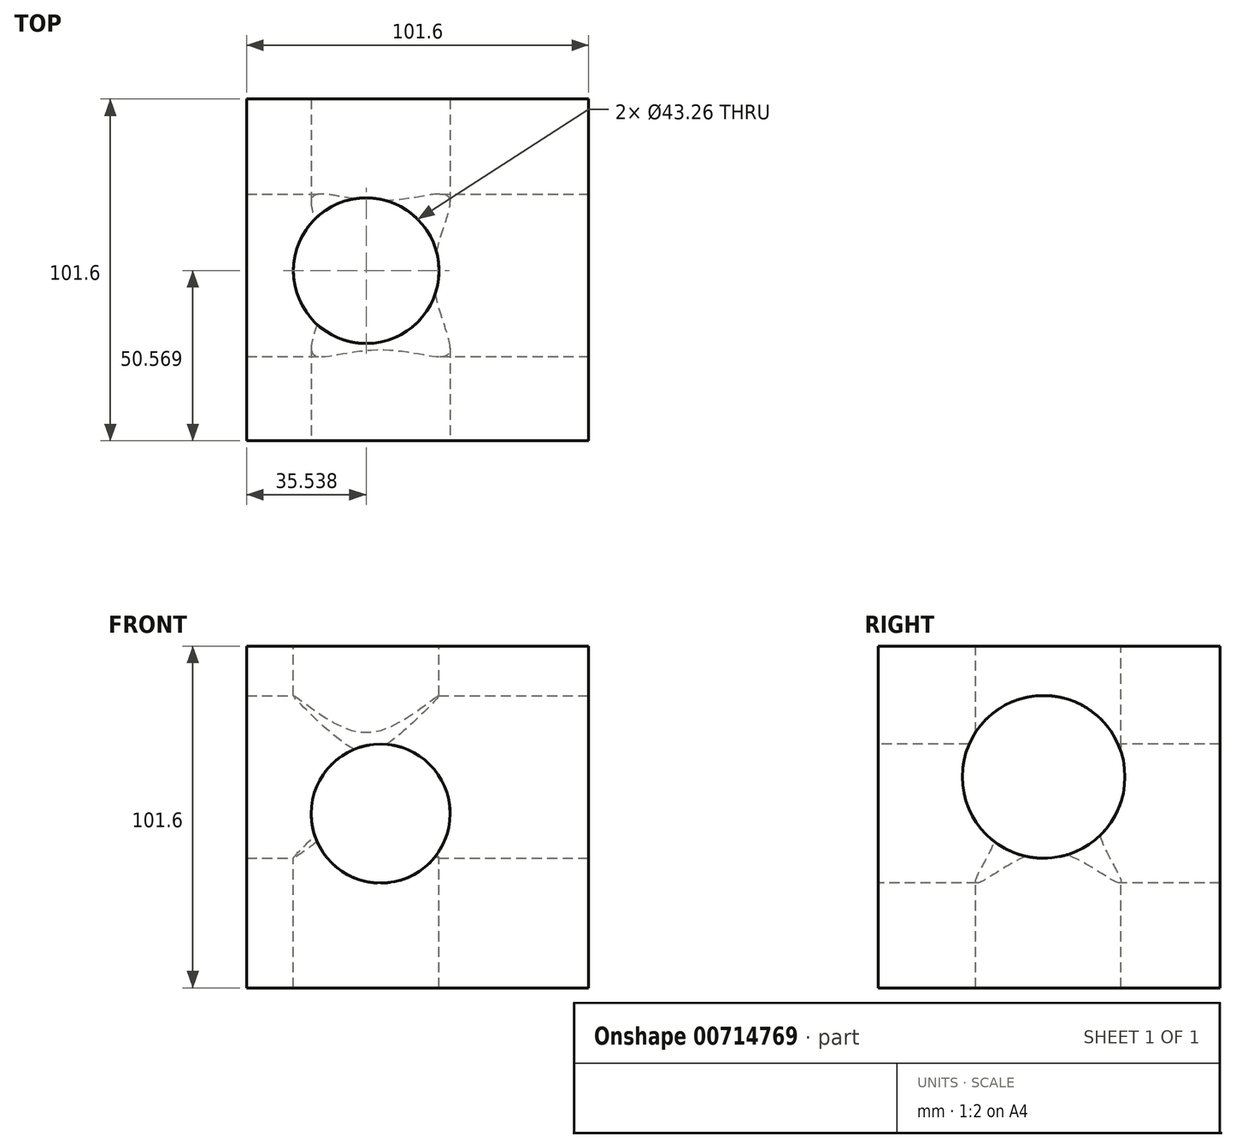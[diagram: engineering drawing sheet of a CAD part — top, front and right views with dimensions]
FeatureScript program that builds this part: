
annotation { "Feature Type Name" : "Feature", "Feature Type Description" : "" }
export const myFeature = defineFeature(function(context is Context, id is Id, definition is map)
    precondition{}
    {
        {
            var Q0;
            Q0=qCreatedBy(makeId("Front.planeOp"),FACE);
            var sketch = newSketch(context, id + "F0", { "sketchPlane" : qUnion([Q0])});
            skLineSegment(sketch, "E0.bottom", {"start": v(-51.94, 58.92) * mm, "end": v(49.66, 58.92) * mm});
            skLineSegment(sketch, "E0.top", {"start": v(-51.94, -42.68) * mm, "end": v(49.66, -42.68) * mm});
            skLineSegment(sketch, "E0.left", {"start": v(-51.94, 58.92) * mm, "end": v(-51.94, -42.68) * mm});
            skLineSegment(sketch, "E0.right", {"start": v(49.66, 58.92) * mm, "end": v(49.66, -42.68) * mm});
            skSolve(sketch);
        }
        {
            var Q0;
            Q0=makeQuery(id+"F0.imprint","IMPRINT",FACE,{"disambiguationData":[TD([[makeQuery(id+"F0.imprint","IMPRINT",EDGE,{"derivedFrom":sQuery(id+"F0.wireOp",EDGE,"E0.bottom")}),-1.0]])]});
            extrude(context, id + "F1", {"entities" : qUnion([Q0]), "depth" : 101.6 * mm, "offsetDistance" : 25.4 * mm});
        }
        {
            var Q0;
            Q0=makeQuery(id+"F1.opExtrude","CAP_FACE",FACE,{"disambiguationData":[OSD([sQuery(id+"F0.wireOp",EDGE,"E0.bottom"),sQuery(id+"F0.wireOp",EDGE,"E0.top"),sQuery(id+"F0.wireOp",EDGE,"E0.left"),sQuery(id+"F0.wireOp",EDGE,"E0.right")])],"isStart":false});
            var sketch = newSketch(context, id + "F2", { "sketchPlane" : qUnion([Q0])});
            skCircle(sketch, "E1", {"center": v(-12.1, 9.11) * mm, "radius": 20.65 * mm});
            skSolve(sketch);
        }
        {
            var Q0;
            Q0=makeQuery(id+"F2.imprint","IMPRINT",FACE,{"disambiguationData":[TD([[makeQuery(id+"F2.imprint","IMPRINT",EDGE,{"derivedFrom":sQuery(id+"F2.wireOp",EDGE,"E1")}),1.0]])]});
            extrude(context, id + "F3", {"entities" : qUnion([Q0]), "operationType" : NewBodyOperationType.REMOVE, "endBound" : BoundingType.THROUGH_ALL, "oppositeDirection" : true, "depth" : 101.6 * mm, "offsetDistance" : 25.4 * mm});
        }
        {
            var Q0;
            Q0=makeQuery(id+"F1.opExtrude","SWEPT_FACE",FACE,{"disambiguationData":[OSD([sQuery(id+"F0.wireOp",EDGE,"E0.right")])]});
            var sketch = newSketch(context, id + "F4", { "sketchPlane" : qUnion([Q0])});
            skCircle(sketch, "E2", {"center": v(-52.4, 20.03) * mm, "radius": 24.17 * mm});
            skSolve(sketch);
        }
        {
            var Q0;
            Q0=makeQuery(id+"F4.imprint","IMPRINT",FACE,{"disambiguationData":[TD([[makeQuery(id+"F4.imprint","IMPRINT",EDGE,{"derivedFrom":sQuery(id+"F4.wireOp",EDGE,"E2")}),1.0]])]});
            extrude(context, id + "F5", {"entities" : qUnion([Q0]), "operationType" : NewBodyOperationType.REMOVE, "endBound" : BoundingType.THROUGH_ALL, "oppositeDirection" : true, "depth" : 101.6 * mm, "offsetDistance" : 25.4 * mm});
        }
        {
            var Q0;
            Q0=makeQuery(id+"F1.opExtrude","SWEPT_FACE",FACE,{"disambiguationData":[OSD([sQuery(id+"F0.wireOp",EDGE,"E0.bottom")])]});
            var sketch = newSketch(context, id + "F6", { "sketchPlane" : qUnion([Q0])});
            skCircle(sketch, "E3", {"center": v(-16.4, -51.03) * mm, "radius": 21.63 * mm});
            skSolve(sketch);
        }
        {
            var Q0;
            Q0=makeQuery(id+"F6.imprint","IMPRINT",FACE,{"disambiguationData":[TD([[makeQuery(id+"F6.imprint","IMPRINT",EDGE,{"derivedFrom":sQuery(id+"F6.wireOp",EDGE,"E3")}),1.0]])]});
            extrude(context, id + "F7", {"entities" : qUnion([Q0]), "operationType" : NewBodyOperationType.REMOVE, "endBound" : BoundingType.THROUGH_ALL, "oppositeDirection" : true, "depth" : 101.6 * mm, "offsetDistance" : 25.4 * mm});
        }
    });
